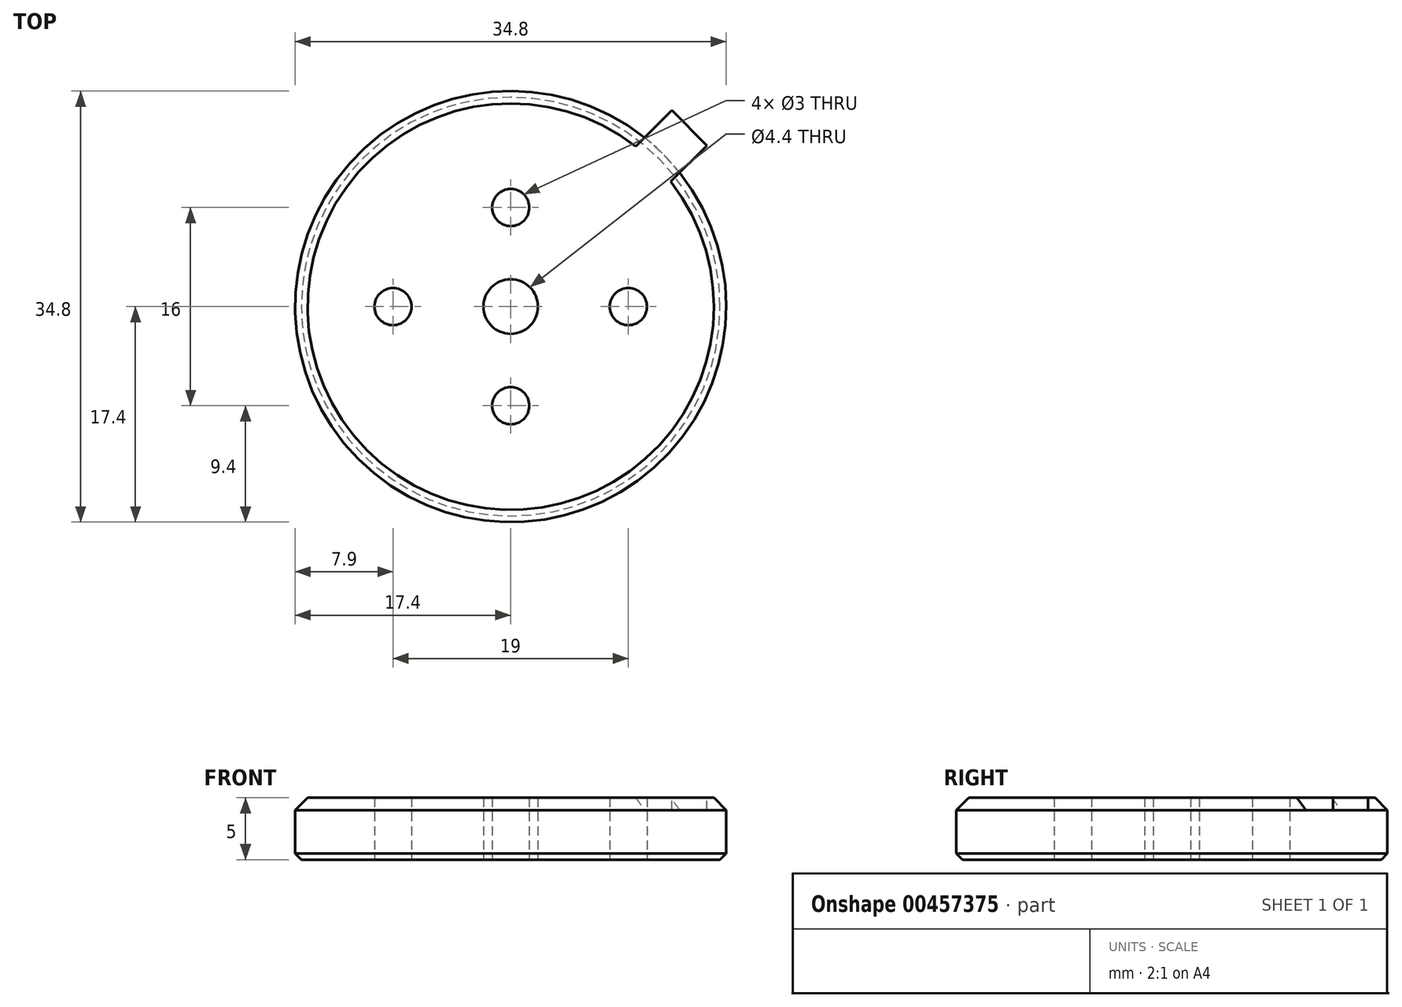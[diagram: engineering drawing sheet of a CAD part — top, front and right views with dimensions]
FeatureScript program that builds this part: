
annotation { "Feature Type Name" : "Feature", "Feature Type Description" : "" }
export const myFeature = defineFeature(function(context is Context, id is Id, definition is map)
    precondition{}
    {
        {
            var Q0;
            Q0=qCreatedBy(makeId("Top.planeOp"),FACE);
            var sketch = newSketch(context, id + "F0", { "sketchPlane" : qUnion([Q0])});
            skCircle(sketch, "E0", {"center": v(0, 0) * mm, "radius": 17.4 * mm});
            skCircle(sketch, "E1", {"center": v(0, 0) * mm, "radius": 2.2 * mm});
            skCircle(sketch, "E2", {"center": v(0, 8) * mm, "radius": 1.5 * mm});
            skCircle(sketch, "E3.1.0", {"center": v(-9.5, 0) * mm, "radius": 1.5 * mm});
            skCircle(sketch, "E3.2.0", {"center": v(0, -8) * mm, "radius": 1.5 * mm});
            skCircle(sketch, "E3.3.0", {"center": v(9.5, 0) * mm, "radius": 1.5 * mm});
            skSolve(sketch);
        }
        {
            var Q0;
            Q0=qSketchRegion(id+"F0",true);
            extrude(context, id + "F1", {"entities" : qUnion([Q0]), "depth" : 5 * mm});
        }
        {
            var Q0;
            Q0=makeQuery(id+"F1.opExtrude","CAP_EDGE",EDGE,{"disambiguationData":[OSD([sQuery(id+"F0.wireOp",EDGE,"E0")])],"isStart":false});
            chamfer(context, id + "F2", {"entities" : qUnion([Q0]), "width" : 1 * mm, "tangentPropagation" : true});
        }
        {
            var Q0;
            Q0=makeQuery(id+"F1.opExtrude","CAP_EDGE",EDGE,{"disambiguationData":[OSD([sQuery(id+"F0.wireOp",EDGE,"E0")])],"isStart":true});
            chamfer(context, id + "F3", {"entities" : qUnion([Q0]), "width" : .5 * mm, "tangentPropagation" : true});
        }
        {
            var Q0;
            Q0=makeQuery(id+"F1.opExtrude","CAP_FACE",FACE,{"disambiguationData":[OSD([sQuery(id+"F0.wireOp",EDGE,"E0"),sQuery(id+"F0.wireOp",EDGE,"E1"),sQuery(id+"F0.wireOp",EDGE,"E2"),sQuery(id+"F0.wireOp",EDGE,"E3.1.0"),sQuery(id+"F0.wireOp",EDGE,"E3.2.0"),sQuery(id+"F0.wireOp",EDGE,"E3.3.0")])],"isStart":false});
            var sketch = newSketch(context, id + "F4", { "sketchPlane" : qUnion([Q0])});
            skLineSegment(sketch, "E4", {"start": v(0, 24.6) * mm, "end": v(24.6, 0) * mm, "construction": true});
            skLineSegment(sketch, "E5", {"start": v(0, 24.6) * mm, "end": v(0, 0) * mm, "construction": true});
            skLineSegment(sketch, "E6", {"start": v(0, 0) * mm, "end": v(24.6, 0) * mm, "construction": true});
            skPoint(sketch, "E7", {"position": v(12.3, 12.3) * mm});
            skLineSegment(sketch, "E8", {"start": v(9.83, 12.66) * mm, "end": v(13.01, 15.84) * mm});
            skLineSegment(sketch, "E9", {"start": v(13.01, 15.84) * mm, "end": v(15.84, 13.01) * mm});
            skLineSegment(sketch, "E10", {"start": v(15.84, 13.01) * mm, "end": v(12.66, 9.83) * mm});
            skLineSegment(sketch, "E11", {"start": v(12.66, 9.83) * mm, "end": v(9.83, 12.66) * mm});
            skSolve(sketch);
        }
        {
            var Q0;
            Q0=qSketchRegion(id+"F4",true);
            extrude(context, id + "F5", {"entities" : qUnion([Q0]), "operationType" : NewBodyOperationType.ADD, "oppositeDirection" : true, "depth" : 1 * mm});
        }
    });
